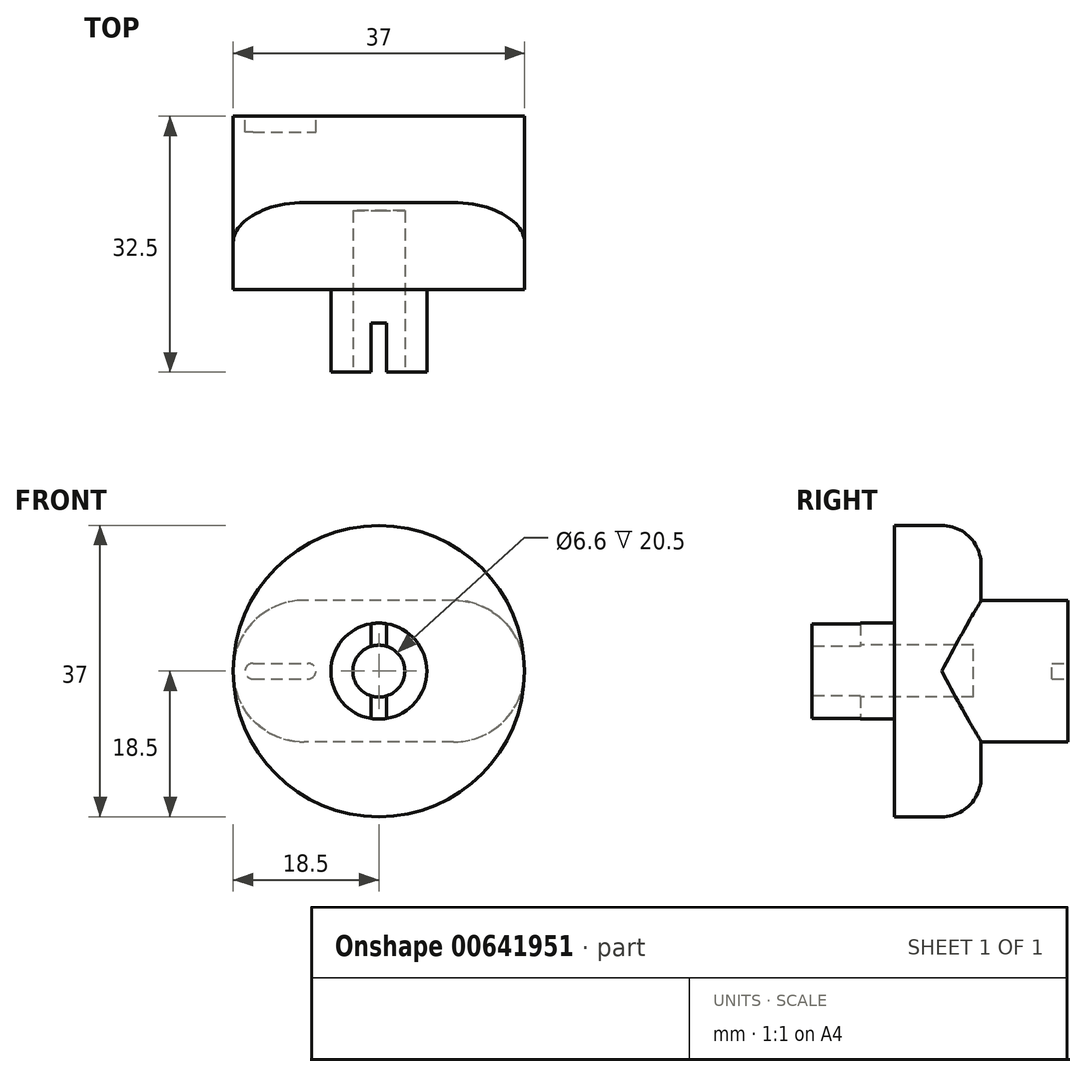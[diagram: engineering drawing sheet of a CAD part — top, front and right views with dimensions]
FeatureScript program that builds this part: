
annotation { "Feature Type Name" : "Feature", "Feature Type Description" : "" }
export const myFeature = defineFeature(function(context is Context, id is Id, definition is map)
    precondition{}
    {
        {
            var Q0;
            Q0=qCreatedBy(makeId("Front.planeOp"),FACE);
            var sketch = newSketch(context, id + "F0", { "sketchPlane" : qUnion([Q0])});
            skCircle(sketch, "E0", {"center": v(0, 0) * mm, "radius": 6.1 * mm});
            skCircle(sketch, "E1", {"center": v(0, 0) * mm, "radius": 3.3 * mm});
            skSolve(sketch);
        }
        {
            var Q0;
            Q0 = qSketchRegion(id + "F0", true);
            extrude(context, id + "F1", {"entities" : qUnion([Q0]), "oppositeDirection" : true, "depth" : 20 * mm, "offsetDistance" : 25 * mm});
        }
        {
            var Q0;
            Q0=qCreatedBy(makeId("Top.planeOp"),FACE);
            var sketch = newSketch(context, id + "F2", { "sketchPlane" : qUnion([Q0])});
            skLineSegment(sketch, "E2", {"start": v(0, 0) * mm, "end": v(0, 38.45) * mm, "construction": true});
            skLineSegment(sketch, "E3", {"start": v(0, 12.5) * mm, "end": v(-18.5, 12.5) * mm});
            skLineSegment(sketch, "E4", {"start": v(0, 12.5) * mm, "end": v(0, 23.5) * mm});
            skLineSegment(sketch, "E5", {"start": v(-18.5, 12.5) * mm, "end": v(-18.5, 18.5) * mm});
            skLineSegment(sketch, "E6", {"start": v(0, 23.5) * mm, "end": v(-13.5, 23.5) * mm});
            skPoint(sketch, "E7.visualSharp", {"position": v(-18.5, 23.5) * mm});
            skArc(sketch, "E7.filletArc", {"start": v(-13.5, 23.5) * mm, "mid": v(-17.04, 22.04) * mm, "end": v(-18.5, 18.5) * mm});
            skSolve(sketch);
        }
        {
            var Q0;
            Q0=makeQuery(id+"F2.imprint","IMPRINT",FACE,{"disambiguationData":[TD([[makeQuery(id+"F2.imprint","IMPRINT",EDGE,{"derivedFrom":sQuery(id+"F2.wireOp",EDGE,"E3")}),-1.0]])]});
            var Q1;
            Q1=sQuery(id+"F2.wireOp",EDGE,"E4");
            revolve(context, id + "F3", {"operationType" : NewBodyOperationType.ADD, "entities" : qUnion([Q0]), "axis" : qUnion([Q1]), "revolveType" : RevolveType.FULL});
        }
        {
            var Q0;
            Q0=makeQuery(id+"F0.imprint","IMPRINT",FACE,{"disambiguationData":[TD([[makeQuery(id+"F0.imprint","IMPRINT",EDGE,{"derivedFrom":sQuery(id+"F0.wireOp",EDGE,"E0")}),1.0]])]});
            extrude(context, id + "F4", {"entities" : qUnion([Q0]), "operationType" : NewBodyOperationType.REMOVE, "oppositeDirection" : true, "depth" : 2 * mm, "offsetDistance" : 25 * mm});
        }
        {
            var Q0;
            Q0=qCreatedBy(makeId("Front.planeOp"),FACE);
            cPlane(context, id + "F5", {"entities" : qUnion([Q0]), "cplaneType" : CPlaneType.OFFSET, "offset" : 12.5 * mm, "oppositeDirection" : true, "width" : 150 * mm, "height" : 150 * mm});
        }
        {
            var Q0;
            Q0=qCreatedBy(id+"F5.planeOp",FACE);
            var sketch = newSketch(context, id + "F6", { "sketchPlane" : qUnion([Q0])});
            skLineSegment(sketch, "E8.bottom", {"start": v(18.5, 9) * mm, "end": v(-18.5, 9) * mm});
            skLineSegment(sketch, "E8.top", {"start": v(18.5, -9) * mm, "end": v(-18.5, -9) * mm});
            skLineSegment(sketch, "E8.left", {"start": v(18.5, 9) * mm, "end": v(18.5, -9) * mm});
            skLineSegment(sketch, "E8.right", {"start": v(-18.5, 9) * mm, "end": v(-18.5, -9) * mm});
            skPoint(sketch, "E8.middle", {"position": v(0, 0) * mm});
            skSolve(sketch);
        }
        {
            var Q0;
            Q0 = qSketchRegion(id + "F6", true);
            extrude(context, id + "F7", {"entities" : qUnion([Q0]), "operationType" : NewBodyOperationType.ADD, "oppositeDirection" : true, "depth" : 22 * mm, "offsetDistance" : 25 * mm});
        }
        {
            var Q0;
            Q0=makeQuery(id+"F7.opExtrude","SWEPT_EDGE",EDGE,{"disambiguationData":[OSD([sQuery(id+"F6.wireOp",EDGE,"E8.top"),sQuery(id+"F6.wireOp",EDGE,"E8.right")])]});
            fillet(context, id + "F8", {"entities" : qUnion([Q0]), "radius" : 9 * mm, "tangentPropagation" : true, "allowEdgeOverflow" : false});
        }
        {
            var Q0;
            Q0=makeQuery(id+"F7.opExtrude","SWEPT_EDGE",EDGE,{"disambiguationData":[OSD([sQuery(id+"F6.wireOp",EDGE,"E8.bottom"),sQuery(id+"F6.wireOp",EDGE,"E8.right")])]});
            fillet(context, id + "F9", {"entities" : qUnion([Q0]), "radius" : 9 * mm, "tangentPropagation" : true, "allowEdgeOverflow" : false});
        }
        {
            var Q0;
            Q0=makeQuery(id+"F7.opExtrude","SWEPT_EDGE",EDGE,{"disambiguationData":[OSD([sQuery(id+"F6.wireOp",EDGE,"E8.top"),sQuery(id+"F6.wireOp",EDGE,"E8.left")])]});
            var Q1;
            Q1=makeQuery(id+"F7.opExtrude","SWEPT_EDGE",EDGE,{"disambiguationData":[OSD([sQuery(id+"F6.wireOp",EDGE,"E8.bottom"),sQuery(id+"F6.wireOp",EDGE,"E8.left")])]});
            fillet(context, id + "F10", {"entities" : qUnion([Q0, Q1]), "radius" : 9 * mm, "tangentPropagation" : true, "allowEdgeOverflow" : false});
        }
        {
            var Q0;
            Q0=makeQuery(id+"F7.opExtrude","CAP_FACE",FACE,{"disambiguationData":[OSD([sQuery(id+"F6.wireOp",EDGE,"E8.bottom"),sQuery(id+"F6.wireOp",EDGE,"E8.top"),sQuery(id+"F6.wireOp",EDGE,"E8.left"),sQuery(id+"F6.wireOp",EDGE,"E8.right")])],"isStart":false});
            cPlane(context, id + "F11", {"entities" : qUnion([Q0]), "cplaneType" : CPlaneType.OFFSET, "offset" : 0 * mm, "oppositeDirection" : true, "width" : 150 * mm, "height" : 150 * mm});
        }
        {
            var Q0;
            Q0=makeQuery(id+"F0.imprint","IMPRINT",FACE,{"disambiguationData":[TD([[makeQuery(id+"F0.imprint","IMPRINT",EDGE,{"derivedFrom":sQuery(id+"F0.wireOp",EDGE,"E0")}),1.0]])]});
            var sketch = newSketch(context, id + "F12", { "sketchPlane" : qUnion([Q0])});
            skLineSegment(sketch, "E9.bottom", {"start": v(-1, 6.5) * mm, "end": v(1, 6.5) * mm});
            skLineSegment(sketch, "E9.top", {"start": v(-1, -6.5) * mm, "end": v(1, -6.5) * mm});
            skLineSegment(sketch, "E9.left", {"start": v(-1, 6.5) * mm, "end": v(-1, -6.5) * mm});
            skLineSegment(sketch, "E9.right", {"start": v(1, 6.5) * mm, "end": v(1, -6.5) * mm});
            skPoint(sketch, "E9.middle", {"position": v(0, 0) * mm});
            skSolve(sketch);
        }
        {
            var Q0;
            Q0 = qSketchRegion(id + "F12", true);
            extrude(context, id + "F13", {"entities" : qUnion([Q0]), "operationType" : NewBodyOperationType.REMOVE, "oppositeDirection" : true, "depth" : 8.2 * mm, "offsetDistance" : 25 * mm});
        }
        {
            var Q0;
            Q0=makeQuery(id+"F6.imprint","IMPRINT",FACE,{"disambiguationData":[TD([[makeQuery(id+"F6.imprint","IMPRINT",EDGE,{"derivedFrom":sQuery(id+"F6.wireOp",EDGE,"E8.bottom")}),1.0]])]});
            var sketch = newSketch(context, id + "F14", { "sketchPlane" : qUnion([Q0])});
            skCircle(sketch, "E10", {"center": v(0, 0) * mm, "radius": 3.3 * mm});
            skSolve(sketch);
        }
        {
            var Q0;
            Q0 = qSketchRegion(id + "F14", true);
            extrude(context, id + "F15", {"entities" : qUnion([Q0]), "operationType" : NewBodyOperationType.REMOVE, "oppositeDirection" : true, "depth" : 10 * mm, "offsetDistance" : 25 * mm});
        }
        {
            var Q0;
            Q0=qCreatedBy(id+"F11.planeOp",FACE);
            var sketch = newSketch(context, id + "F16", { "sketchPlane" : qUnion([Q0])});
            skLineSegment(sketch, "E11", {"start": v(16, 0) * mm, "end": v(9, 0) * mm});
            skArc(sketch, "E12.0.startCap", {"start": v(16, 1) * mm, "mid": v(17, 0) * mm, "end": v(16, -1) * mm});
            skArc(sketch, "E12.0.endCap", {"start": v(9, -1) * mm, "mid": v(8, 0) * mm, "end": v(9, 1) * mm});
            skLineSegment(sketch, "E12.0.left", {"start": v(16, -1) * mm, "end": v(9, -1) * mm});
            skLineSegment(sketch, "E12.0.right", {"start": v(16, 1) * mm, "end": v(9, 1) * mm});
            skSolve(sketch);
        }
        {
            var Q0;
            Q0 = qSketchRegion(id + "F16", true);
            extrude(context, id + "F17", {"entities" : qUnion([Q0]), "operationType" : NewBodyOperationType.REMOVE, "oppositeDirection" : true, "depth" : 2 * mm, "offsetDistance" : 25 * mm});
        }
    });
